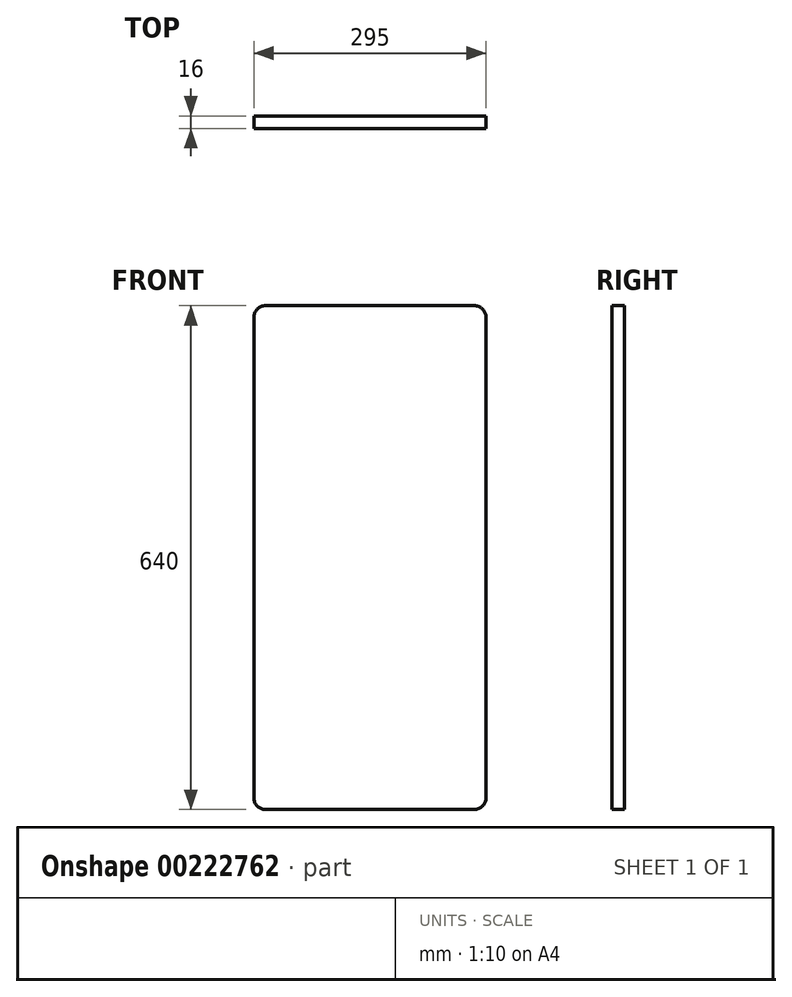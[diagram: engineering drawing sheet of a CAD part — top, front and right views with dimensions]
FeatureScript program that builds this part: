
annotation { "Feature Type Name" : "Feature", "Feature Type Description" : "" }
export const myFeature = defineFeature(function(context is Context, id is Id, definition is map)
    precondition{}
    {
        {
            var Q0;
            Q0=qCreatedBy(makeId("Front.planeOp"),FACE);
            var sketch = newSketch(context, id + "F0", { "sketchPlane" : qUnion([Q0])});
            skLineSegment(sketch, "E0.bottom", {"start": v(15, 640) * mm, "end": v(280, 640) * mm});
            skLineSegment(sketch, "E0.top", {"start": v(15, 0) * mm, "end": v(280, 0) * mm});
            skLineSegment(sketch, "E0.left", {"start": v(0, 625) * mm, "end": v(0, 15) * mm});
            skLineSegment(sketch, "E0.right", {"start": v(295, 625) * mm, "end": v(295, 15) * mm});
            skPoint(sketch, "E1.visualSharp", {"position": v(0, 640) * mm});
            skArc(sketch, "E1.filletArc", {"start": v(15, 640) * mm, "mid": v(4.4, 635.6) * mm, "end": v(0, 625) * mm});
            skPoint(sketch, "E2.visualSharp", {"position": v(295, 640) * mm});
            skArc(sketch, "E2.filletArc", {"start": v(295, 625) * mm, "mid": v(290.6, 635.6) * mm, "end": v(280, 640) * mm});
            skPoint(sketch, "E3.visualSharp", {"position": v(295, 0) * mm});
            skArc(sketch, "E3.filletArc", {"start": v(280, 0) * mm, "mid": v(290.6, 4.4) * mm, "end": v(295, 15) * mm});
            skPoint(sketch, "E4.visualSharp", {"position": v(0, 0) * mm});
            skArc(sketch, "E4.filletArc", {"start": v(0, 15) * mm, "mid": v(4.4, 4.4) * mm, "end": v(15, 0) * mm});
            skSolve(sketch);
        }
        {
            var Q0;
            Q0=makeQuery(id+"F0.imprint","IMPRINT",FACE,{"disambiguationData":[TD([[makeQuery(id+"F0.imprint","IMPRINT",EDGE,{"derivedFrom":sQuery(id+"F0.wireOp",EDGE,"E0.bottom")}),-1.0]])]});
            extrude(context, id + "F1", {"entities" : qUnion([Q0]), "depth" : 16 * mm});
        }
    });
